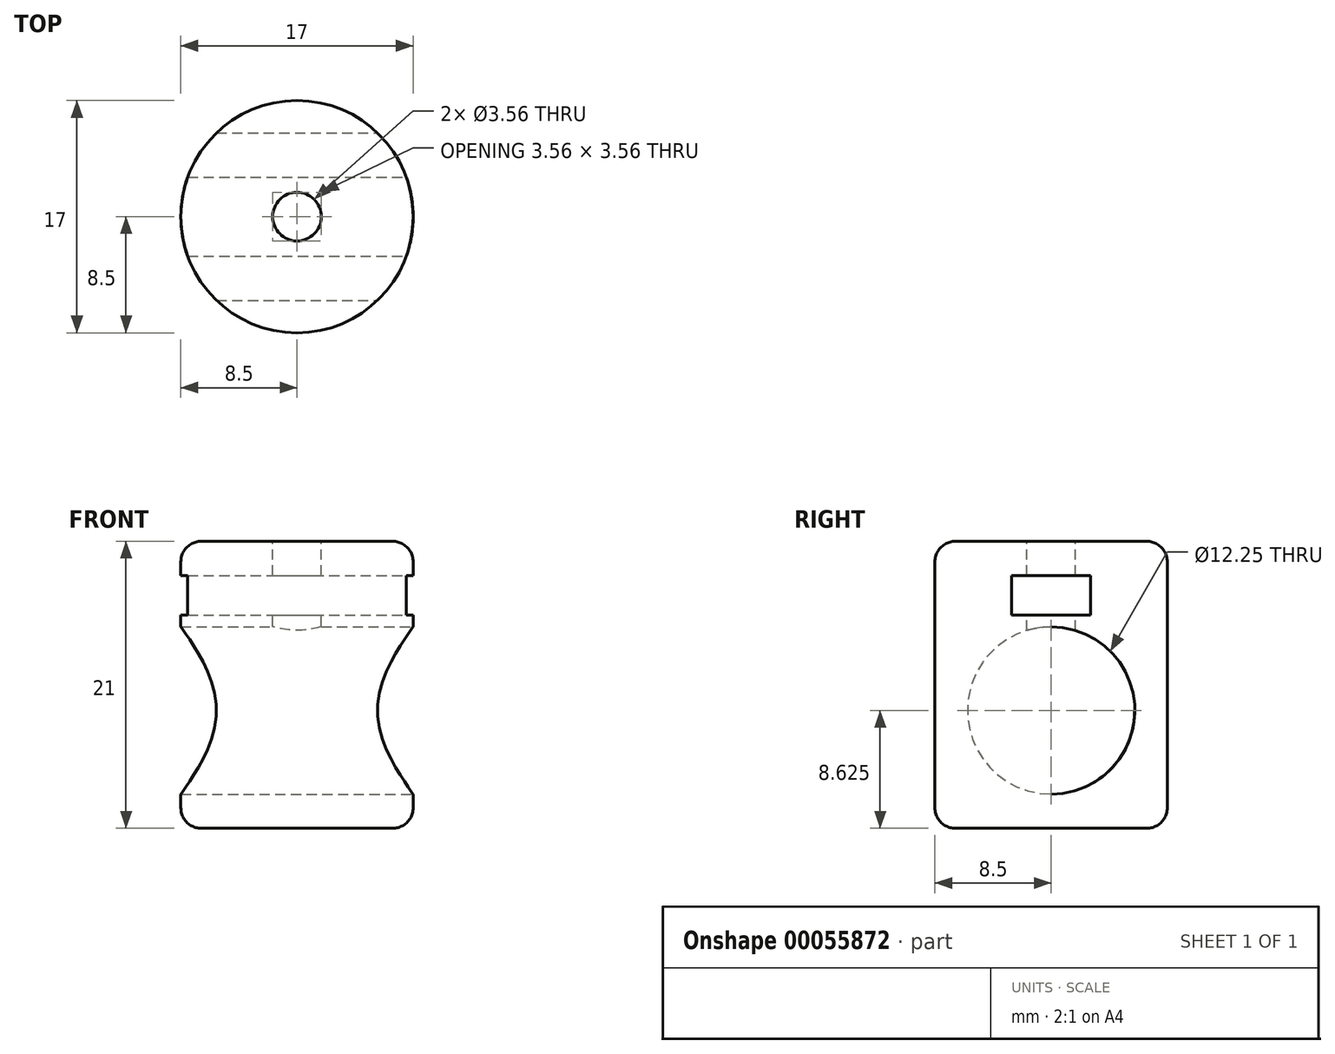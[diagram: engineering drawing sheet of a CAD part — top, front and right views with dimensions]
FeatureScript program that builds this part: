
annotation { "Feature Type Name" : "Feature", "Feature Type Description" : "" }
export const myFeature = defineFeature(function(context is Context, id is Id, definition is map)
    precondition{}
    {
        {
            var Q0;
            Q0=qCreatedBy(makeId("Top.planeOp"),FACE);
            var sketch = newSketch(context, id + "F0", { "sketchPlane" : qUnion([Q0])});
            skCircle(sketch, "E0", {"center": v(0, 0) * mm, "radius": 8.5 * mm});
            skSolve(sketch);
        }
        {
            var Q0;
            Q0=qSketchRegion(id+"F0",true);
            extrude(context, id + "F1", {"entities" : qUnion([Q0]), "depth" : 21 * mm});
        }
        {
            var Q0;
            Q0=qCreatedBy(makeId("Right.planeOp"),FACE);
            var sketch = newSketch(context, id + "F2", { "sketchPlane" : qUnion([Q0])});
            skCircle(sketch, "E1", {"center": v(0, 8.62) * mm, "radius": 6.12 * mm});
            skSolve(sketch);
        }
        {
            var Q0;
            Q0=qSketchRegion(id+"F2",true);
            extrude(context, id + "F3", {"entities" : qUnion([Q0]), "operationType" : NewBodyOperationType.REMOVE, "endBound" : BoundingType.THROUGH_ALL, "oppositeDirection" : true, "depth" : 25.4 * mm, "hasSecondDirection" : true, "secondDirectionOppositeDirection" : false, "secondDirectionDepth" : 25.4 * mm});
        }
        {
            var Q0;
            Q0=makeQuery(id+"F1.opExtrude","CAP_EDGE",EDGE,{"disambiguationData":[OSD([sQuery(id+"F0.wireOp",EDGE,"E0")])],"isStart":true});
            var Q1;
            Q1=makeQuery(id+"F1.opExtrude","CAP_EDGE",EDGE,{"disambiguationData":[OSD([sQuery(id+"F0.wireOp",EDGE,"E0")])],"isStart":false});
            fillet(context, id + "F4", {"entities" : qUnion([Q0, Q1]), "radius" : 1.5 * mm, "tangentPropagation" : true, "allowEdgeOverflow" : false});
        }
        {
            var Q0;
            Q0=qCreatedBy(makeId("Right.planeOp"),FACE);
            var sketch = newSketch(context, id + "F5", { "sketchPlane" : qUnion([Q0])});
            skLineSegment(sketch, "E2.bottom", {"start": v(-2.9, 18.5) * mm, "end": v(2.9, 18.5) * mm});
            skLineSegment(sketch, "E2.top", {"start": v(-2.9, 15.6) * mm, "end": v(2.9, 15.6) * mm});
            skLineSegment(sketch, "E2.left", {"start": v(-2.9, 18.5) * mm, "end": v(-2.9, 15.6) * mm});
            skLineSegment(sketch, "E2.right", {"start": v(2.9, 18.5) * mm, "end": v(2.9, 15.6) * mm});
            skSolve(sketch);
        }
        {
            var Q0;
            Q0=qSketchRegion(id+"F5",true);
            extrude(context, id + "F6", {"entities" : qUnion([Q0]), "operationType" : NewBodyOperationType.REMOVE, "oppositeDirection" : true, "depth" : 25.4 * mm, "hasSecondDirection" : true, "secondDirectionOppositeDirection" : false, "secondDirectionDepth" : 25.4 * mm});
        }
        {
            var Q0;
            Q0=makeQuery(id+"F1.opExtrude","CAP_FACE",FACE,{"disambiguationData":[OSD([sQuery(id+"F0.wireOp",EDGE,"E0")])],"isStart":false});
            var sketch = newSketch(context, id + "F7", { "sketchPlane" : qUnion([Q0])});
            skCircle(sketch, "E3", {"center": v(0, 0) * mm, "radius": 1.78 * mm});
            skSolve(sketch);
        }
        {
            var Q0;
            Q0=qSketchRegion(id+"F7",true);
            extrude(context, id + "F8", {"entities" : qUnion([Q0]), "operationType" : NewBodyOperationType.REMOVE, "oppositeDirection" : true, "depth" : 10 * mm});
        }
    });
